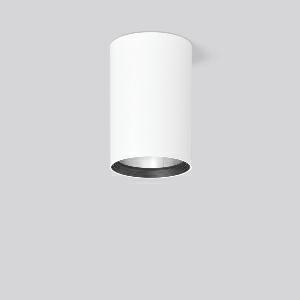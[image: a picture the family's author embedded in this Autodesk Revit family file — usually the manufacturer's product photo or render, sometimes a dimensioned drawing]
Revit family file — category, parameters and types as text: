
# Revit family: heledon_maxi_a_931231_002_76_4753
name_source: partatom
category: Lighting Fixtures
units: mm (PartAtom-declared; Revit-internal decimal feet)

## family parameters
Cut with Voids When Loaded = No
Host = Face
Light Source = No
Part Type = Normal
Room Calculation Point = No
Round Connector Dimension = Use Diameter
Shared = No

## types (1)
- HELEDON maxi A (1 x LED Modul 932 fresh meat, 2150 lm, 3200)
    Apparent Load = 33 VA
    Approval mark = CE
    CIE Flux Codes = 100 100 100 100 100
    Color Rendering = 90
    Color Temperature = 3200
    Default Elevation = 1800 mm
    Description = Series: HELEDON maxi
Cylindrical surface-mounted downlight. Housing: die-cast aluminium, powder-coated. Internal ceiling frame polycarbonate with bayonet mounting. Black plastic ring and recessed LED to prevent glare from the side. Optical assembly with reflector made of MIRO-Silver with 98% total light reflection for outstanding efficiency - can be changed without tools. Special LED for illumination of meat included. Suitable for Ceiling mounting. Easy installation with a separate ceiling frame with bayonet mounting and plug connection. Driver integrated. Connected via plug-in connector. High quality converter without flickering and stroboscopic effect. The following accessories can be mounted without use of tools: interchangeable lenses, decorative glasses, honeycomb louvre, clear and frosted diffusers, white interchangeable plastic ring. 
Colour: traffic white, matt (RAL 9016)
Diameter: 123 mm
Height: 183 mm
Lamp: LED
Socket: without socket
Colour temperature: fresh meat
System power: 33 W
Rated luminous flux: 2150 lm
Luminous efficiency: 65 lm/W
Control gear: Converter, dimmable, DALI
Protection class: I
Type of protection: IP 20
    Height = 183 mm
    Lamp = 1 x LED Modul 932 fresh meat
    Lamp Light Flux = 2150 lm
    Lamp count = 1
    Length = 123 mm
    Lifetime = 50000 h
    Luminous efficacy = 65 lm/W
    Manufacturer = RZB
    ModVariant = No
    Model = 931231.002.76
    Mounting Place = Ceiling
    Mounting Type = Surface mounted
    Number of Poles = 1
    OnlyDefault = Yes
    Power Factor = 1
    Product Name = HELEDON maxi A
    Product group = Surface mounted downlights
    ProductGroupID = 302
    Protection Class = Protection class I
    Protection Degree = IP 20
    RLX_Detail_Level = 1
    RLX_Emergency_Light_Flux = 0 lm
    RLX_Emergency_Type = 0
    RLX_Emergency_Type_DB = No
    RlxData = <blob elided: 96969 chars, md5=85eb4162>
    Socket = socket
    Standby Power = 0 W
    System Light Flux = 2150 lm
    System Power = 33 W
    Type Comments = Product without accessories
    Type Image = 931192.002.jpg
    URL = http://relux.com
    VarID = ---
    Voltage = 230 V
    Voltage Range = 220-240 V
    Weight = 0.00 kg
    Width = 0 mm  [stored 0 ft]

note: [stored X ft] marks values corroborated as IEEE doubles in the binary element streams (Revit-internal decimal feet)

## geometry (parser evidence)
native form markers: Blend x4, Sweep x11
no freeform markers — native parametric forms only
